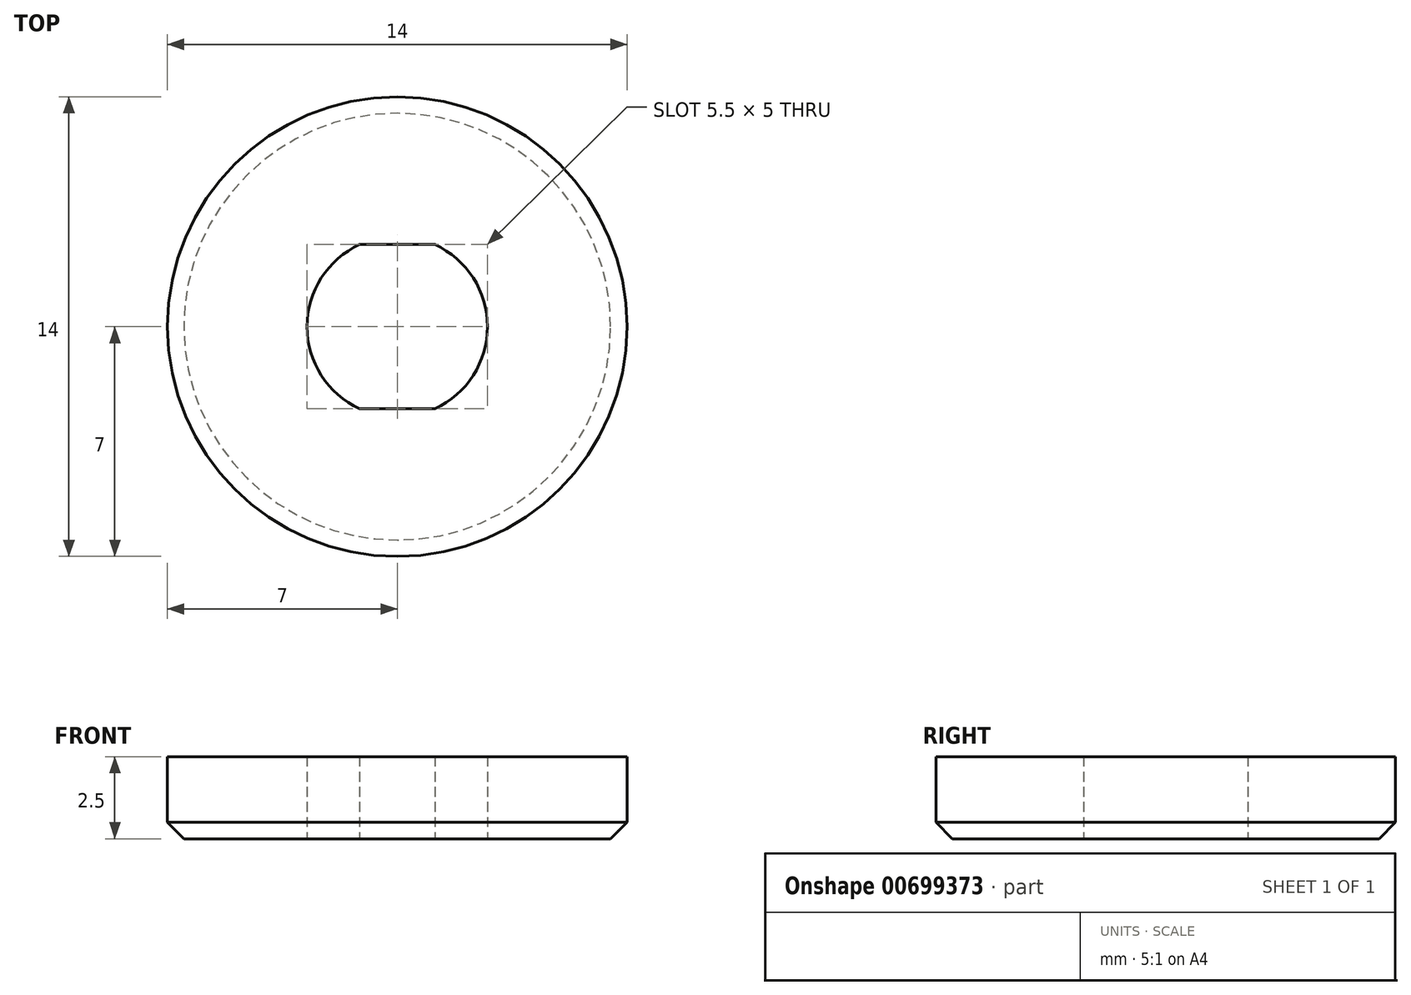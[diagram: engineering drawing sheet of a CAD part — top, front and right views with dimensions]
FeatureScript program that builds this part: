
annotation { "Feature Type Name" : "Feature", "Feature Type Description" : "" }
export const myFeature = defineFeature(function(context is Context, id is Id, definition is map)
    precondition{}
    {
        {
            var Q0;
            Q0=qCreatedBy(makeId("Top.planeOp"),FACE);
            var sketch = newSketch(context, id + "F0", { "sketchPlane" : qUnion([Q0])});
            skCircle(sketch, "E0", {"center": v(0, 0) * mm, "radius": 7 * mm});
            skArc(sketch, "E1", {"start": v(-1.15, 2.5) * mm, "mid": v(-2.75, 0) * mm, "end": v(-1.15, -2.5) * mm});
            skLineSegment(sketch, "E2.bottom", {"start": v(-1.15, 2.5) * mm, "end": v(1.15, 2.5) * mm});
            skLineSegment(sketch, "E2.top", {"start": v(-1.15, -2.5) * mm, "end": v(1.15, -2.5) * mm});
            skArc(sketch, "E3.trimOffspring", {"start": v(1.15, -2.5) * mm, "mid": v(2.75, 0) * mm, "end": v(1.15, 2.5) * mm});
            skPoint(sketch, "E4.orphan", {"position": v(-3, 2.5) * mm});
            skPoint(sketch, "E5.orphan", {"position": v(-3, -2.5) * mm});
            skPoint(sketch, "E2.right.end.orphan", {"position": v(3, -2.5) * mm});
            skPoint(sketch, "E6.orphan", {"position": v(3, 2.5) * mm});
            skSolve(sketch);
        }
        {
            var Q0;
            Q0=makeQuery(id+"F0.imprint","IMPRINT",FACE,{"disambiguationData":[TD([[makeQuery(id+"F0.imprint","IMPRINT",EDGE,{"derivedFrom":sQuery(id+"F0.wireOp",EDGE,"E0")}),1.0]])]});
            extrude(context, id + "F1", {"entities" : qUnion([Q0]), "depth" : 2.5 * mm, "offsetDistance" : 25 * mm});
        }
        {
            var Q0;
            Q0=makeQuery(id+"F1.opExtrude","CAP_EDGE",EDGE,{"disambiguationData":[OSD([sQuery(id+"F0.wireOp",EDGE,"E0")])],"isStart":true});
            chamfer(context, id + "F2", {"entities" : qUnion([Q0]), "width" : .5 * mm, "tangentPropagation" : true});
        }
    });
